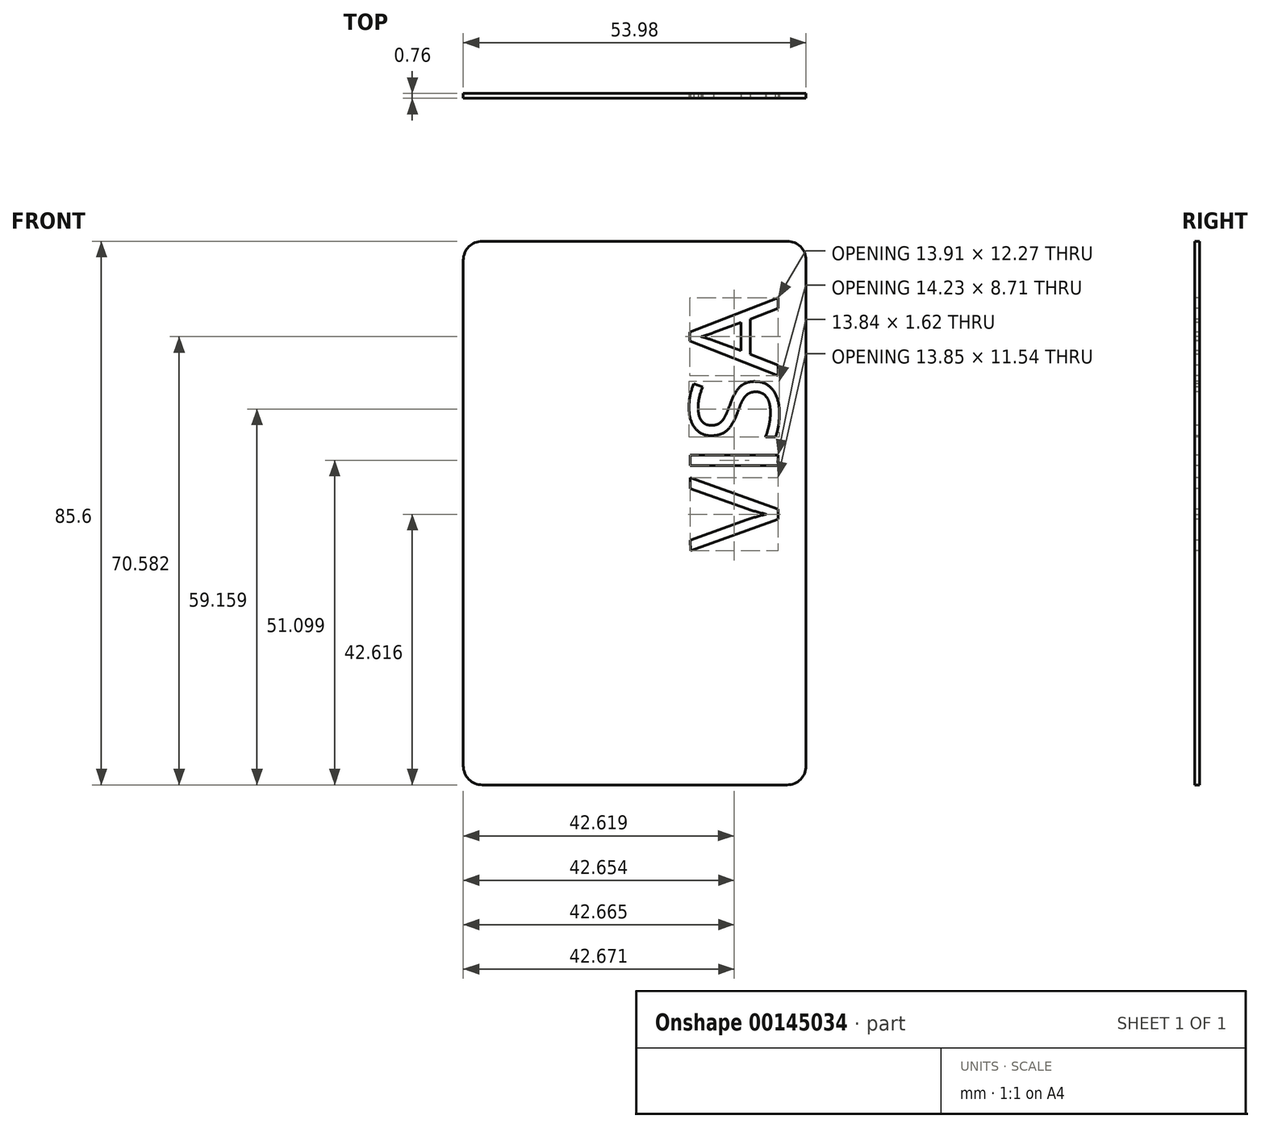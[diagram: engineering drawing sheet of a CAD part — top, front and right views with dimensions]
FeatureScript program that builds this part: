
annotation { "Feature Type Name" : "Feature", "Feature Type Description" : "" }
export const myFeature = defineFeature(function(context is Context, id is Id, definition is map)
    precondition{}
    {
        {
            var Q0;
            Q0=qCreatedBy(makeId("Front.planeOp"),FACE);
            var sketch = newSketch(context, id + "F0", { "sketchPlane" : qUnion([Q0])});
            skLineSegment(sketch, "E0.bottom", {"start": v(-3, 0) * mm, "end": v(-50.98, 0) * mm});
            skLineSegment(sketch, "E0.top", {"start": v(-3, 85.6) * mm, "end": v(-50.98, 85.6) * mm});
            skLineSegment(sketch, "E0.left", {"start": v(0, 3) * mm, "end": v(0, 82.6) * mm});
            skLineSegment(sketch, "E0.right", {"start": v(-53.98, 3) * mm, "end": v(-53.98, 82.6) * mm});
            skPoint(sketch, "E1.visualSharp", {"position": v(-53.98, 85.6) * mm});
            skArc(sketch, "E1.filletArc", {"start": v(-50.98, 85.6) * mm, "mid": v(-53.1, 84.72) * mm, "end": v(-53.98, 82.6) * mm});
            skPoint(sketch, "E2.visualSharp", {"position": v(0, 85.6) * mm});
            skArc(sketch, "E2.filletArc", {"start": v(0, 82.6) * mm, "mid": v(-0.88, 84.72) * mm, "end": v(-3, 85.6) * mm});
            skPoint(sketch, "E3.visualSharp", {"position": v(0, 0) * mm});
            skArc(sketch, "E3.filletArc", {"start": v(-3, 0) * mm, "mid": v(-0.88, 0.88) * mm, "end": v(0, 3) * mm});
            skPoint(sketch, "E4.visualSharp", {"position": v(-53.98, 0) * mm});
            skArc(sketch, "E4.filletArc", {"start": v(-53.98, 3) * mm, "mid": v(-53.1, 0.88) * mm, "end": v(-50.98, 0) * mm});
            skSolve(sketch);
        }
        {
            var Q0;
            Q0=makeQuery(id+"F0.imprint","IMPRINT",FACE,{"disambiguationData":[TD([[makeQuery(id+"F0.imprint","IMPRINT",EDGE,{"derivedFrom":sQuery(id+"F0.wireOp",EDGE,"E0.bottom")}),-1.0]])]});
            extrude(context, id + "F1", {"entities" : qUnion([Q0]), "depth" : 0.76 * mm});
        }
        {
            var Q0;
            Q0=makeQuery(id+"F1.opExtrude","CAP_FACE",FACE,{"disambiguationData":[OSD([sQuery(id+"F0.wireOp",EDGE,"E0.bottom"),sQuery(id+"F0.wireOp",EDGE,"E0.top"),sQuery(id+"F0.wireOp",EDGE,"E0.left"),sQuery(id+"F0.wireOp",EDGE,"E0.right"),sQuery(id+"F0.wireOp",EDGE,"E1.filletArc"),sQuery(id+"F0.wireOp",EDGE,"E2.filletArc"),sQuery(id+"F0.wireOp",EDGE,"E3.filletArc"),sQuery(id+"F0.wireOp",EDGE,"E4.filletArc")])],"isStart":false});
            var sketch = newSketch(context, id + "F2", { "sketchPlane" : qUnion([Q0])});
            skText(sketch, "E5", { "text": "VISA", "fontName": "OpenSans-Regular.ttf"});
            const initialGuessF2  = {"E5": [-0.00438, 0.03686, -0.001, 1, 0.01396]};
            skSetInitialGuess(sketch, initialGuessF2);
            skSolve(sketch);
        }
        {
            var Q0;
            Q0 = qSketchRegion(id + "F2", true);
            extrude(context, id + "F3", {"entities" : qUnion([Q0]), "operationType" : NewBodyOperationType.REMOVE, "endBound" : BoundingType.THROUGH_ALL, "oppositeDirection" : true, "depth" : .5 * mm});
        }
    });
